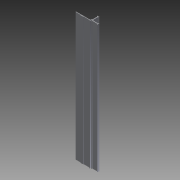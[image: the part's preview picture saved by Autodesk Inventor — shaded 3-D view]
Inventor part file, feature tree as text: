
AUTODESK INVENTOR PART (.ipt)
format: ipt  version: 2016 (Build 200138000, 138)  size: 133,632 bytes
history: native  units: mm
features: other x63, extrude x1, sketch x1
ambient origin geometry x8: Origin, YZ Plane, XZ Plane, XY Plane, X Axis, Y Axis, Z Axis, Center Point
bodies: Solid1 (feature_tree)
feature tree (65):
  extrude  "Extrusion1"  [1 undecoded]
  other  "start_XY"
  other  "start_YZ"
  other  "start_ZX"
  other  "start_X"
  other  "start_Y"
  other  "start_Z"
  other  "start_Center"
  other  "end_XY"
  other  "end_YZ"
  other  "end_ZX"
  other  "end_X"
  other  "end_Y"
  other  "end_Z"
  other  "end_Center"
  other  "side_1a_XY"
  other  "side_1a_YZ"
  other  "side_1a_ZX"
  other  "side_1a_X"
  other  "side_1a_Y"
  other  "side_1a_Z"
  other  "side_1a_Center"
  other  "side_1b_XY"
  other  "side_1b_YZ"
  other  "side_1b_ZX"
  other  "side_1b_X"
  other  "side_1b_Y"
  other  "side_1b_Z"
  other  "side_1b_Center"
  other  "side_1_XY"
  other  "side_1_YZ"
  other  "side_1_ZX"
  other  "side_1_X"
  other  "side_1_Y"
  other  "side_1_Z"
  other  "side_1_Center"
  other  "side_6a_XY"
  other  "side_6a_YZ"
  other  "side_6a_ZX"
  other  "side_6a_X"
  other  "side_6a_Y"
  other  "side_6a_Z"
  other  "side_6a_Center"
  other  "side_2_XY"
  other  "side_2_YZ"
  other  "side_2_ZX"
  other  "side_2_X"
  other  "side_2_Y"
  other  "side_2_Z"
  other  "side_2_Center"
  other  "side_5_XY"
  other  "side_5_YZ"
  other  "side_5_ZX"
  other  "side_5_X"
  other  "side_5_Y"
  other  "side_5_Z"
  other  "side_5_Center"
  other  "side_6_XY"
  other  "side_6_YZ"
  other  "side_6_ZX"
  other  "side_6_X"
  other  "side_6_Y"
  other  "side_6_Z"
  other  "side_6_Center"
  sketch  "Skizze_1"  dims[d0=329.0mm d1=0.0mm]
note: 1 required parameter value undecoded (feature->parameter linkage not recoverable at this tier; creation-order binding heuristic only, values carry confidence <= 0.55)
